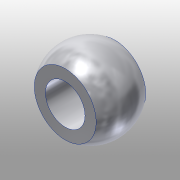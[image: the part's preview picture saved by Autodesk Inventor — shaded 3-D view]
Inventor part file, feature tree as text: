
AUTODESK INVENTOR PART (.ipt)
format: ipt  version: 2015 (Build 190159000, 159)  size: 123,392 bytes
history: native  units: mm
features: other x3, sketch x3
ambient origin geometry x8: Origin, YZ Plane, XZ Plane, XY Plane, X Axis, Y Axis, Z Axis, Center Point
bodies: Solid1 (feature_tree)
feature tree (6):
  other  "500-109.ipt"
  other  "Solid1::500-109.ipt"
  other  "TaggingFeature1"
  sketch  "Sketch1"  dims[d0=10.0mm]
  sketch  "Sketch2"
  sketch  "Sketch3"
